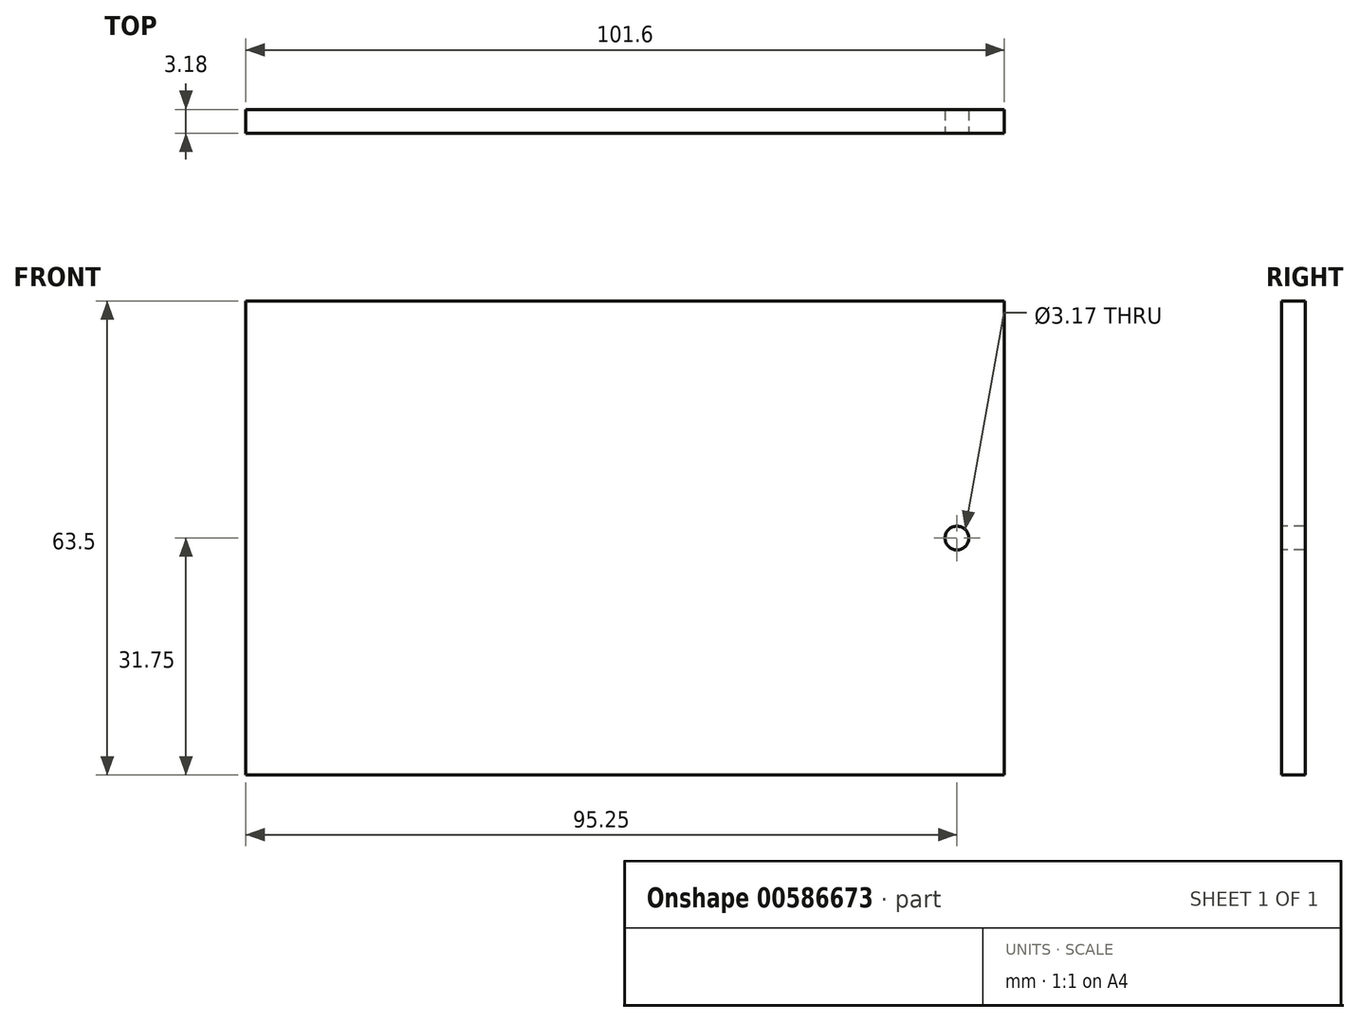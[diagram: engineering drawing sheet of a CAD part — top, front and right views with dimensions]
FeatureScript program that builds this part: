
annotation { "Feature Type Name" : "Feature", "Feature Type Description" : "" }
export const myFeature = defineFeature(function(context is Context, id is Id, definition is map)
    precondition{}
    {
        {
            var Q0;
            Q0=qCreatedBy(makeId("Front.planeOp"),FACE);
            var sketch = newSketch(context, id + "F0", { "sketchPlane" : qUnion([Q0])});
            skLineSegment(sketch, "E0.bottom", {"start": v(0, 0) * mm, "end": v(101.6, 0) * mm});
            skLineSegment(sketch, "E0.top", {"start": v(0, 63.5) * mm, "end": v(101.6, 63.5) * mm});
            skLineSegment(sketch, "E0.left", {"start": v(0, 0) * mm, "end": v(0, 63.5) * mm});
            skLineSegment(sketch, "E0.right", {"start": v(101.6, 0) * mm, "end": v(101.6, 63.5) * mm});
            skSolve(sketch);
        }
        {
            var Q0;
            Q0 = qSketchRegion(id + "F0", true);
            extrude(context, id + "F1", {"entities" : qUnion([Q0]), "depth" : 3.17 * mm, "offsetDistance" : 25.4 * mm});
        }
        {
            var Q0;
            Q0=makeQuery(id+"F1.opExtrude","CAP_FACE",FACE,{"disambiguationData":[OSD([sQuery(id+"F0.wireOp",EDGE,"E0.bottom"),sQuery(id+"F0.wireOp",EDGE,"E0.top"),sQuery(id+"F0.wireOp",EDGE,"E0.left"),sQuery(id+"F0.wireOp",EDGE,"E0.right")])],"isStart":false});
            var sketch = newSketch(context, id + "F2", { "sketchPlane" : qUnion([Q0])});
            skPoint(sketch, "E1", {"position": v(95.25, 31.75) * mm});
            skLineSegment(sketch, "E2", {"start": v(0, 31.75) * mm, "end": v(2.48, 31.75) * mm, "construction": true});
            skSolve(sketch);
        }
        {
            var Q0;
            Q0=sQuery(id+"F2.wireOp",VERTEX,"E1");
            var Q1;
            Q1=makeQuery(id+"F1.opExtrude","SWEPT_BODY",BODY,{"disambiguationData":[OSD([sQuery(id+"F0.wireOp",EDGE,"E0.bottom"),sQuery(id+"F0.wireOp",EDGE,"E0.top"),sQuery(id+"F0.wireOp",EDGE,"E0.left"),sQuery(id+"F0.wireOp",EDGE,"E0.right")])]});
            hole(context, id + "F3", {"style" : HoleStyle.SIMPLE, "endStyle" : HoleEndStyle.THROUGH, "holeDiameter" : 3.17 * mm, "majorDiameter" : 6.35 * mm, "isTappedThrough" : true, "tappedDepth" : 12.7 * mm, "tapClearance" : 3, "locations" : qUnion([Q0]), "scope" : qUnion([Q1])});
        }
    });
